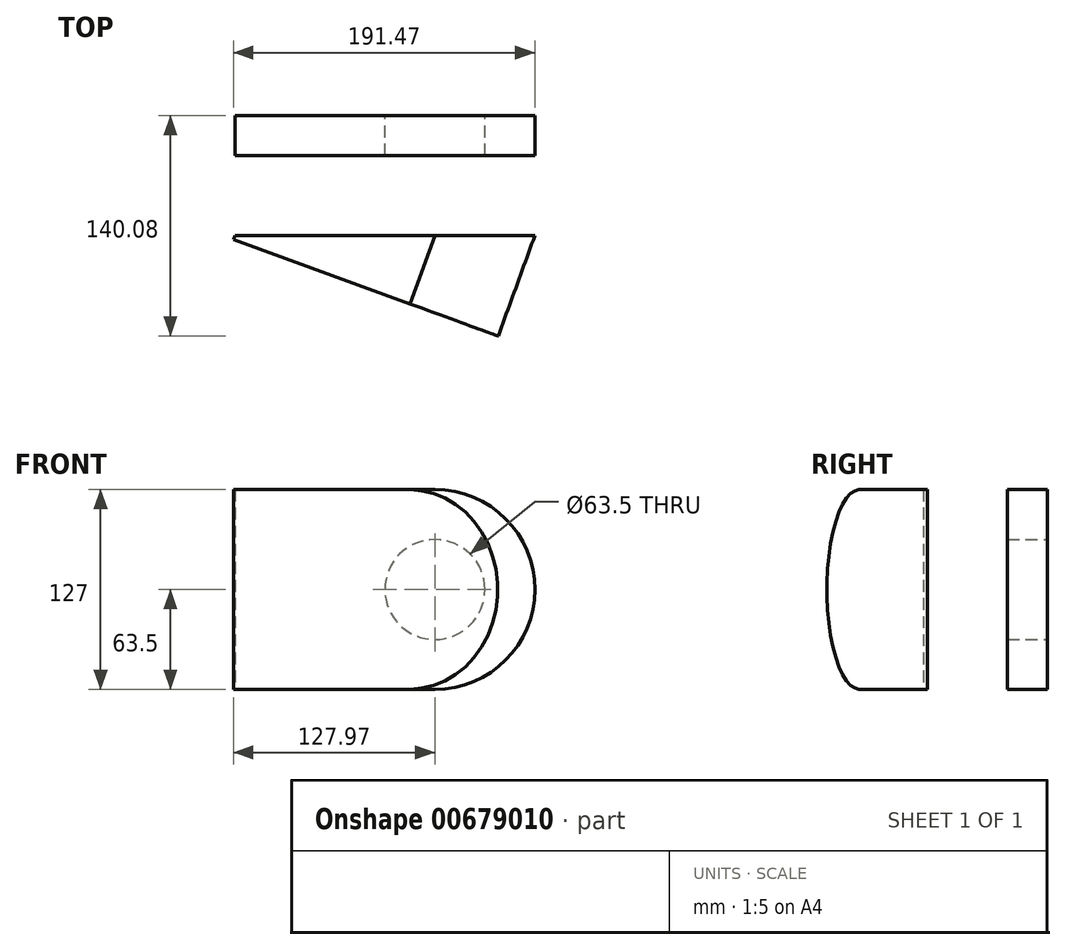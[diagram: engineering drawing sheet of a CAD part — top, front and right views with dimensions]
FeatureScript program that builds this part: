
annotation { "Feature Type Name" : "Feature", "Feature Type Description" : "" }
export const myFeature = defineFeature(function(context is Context, id is Id, definition is map)
    precondition{}
    {
        {
            var Q0;
            Q0=qCreatedBy(makeId("Front.planeOp"),FACE);
            var sketch = newSketch(context, id + "F0", { "sketchPlane" : qUnion([Q0])});
            skArc(sketch, "E0", {"start": v(0, -63.5) * mm, "mid": v(63.5, 0) * mm, "end": v(0, 63.5) * mm});
            skCircle(sketch, "E1", {"center": v(0, 0) * mm, "radius": 31.75 * mm});
            skLineSegment(sketch, "E2", {"start": v(0, 63.5) * mm, "end": v(-127, 63.5) * mm});
            skLineSegment(sketch, "E3", {"start": v(-127, 63.5) * mm, "end": v(-127, -63.5) * mm});
            skLineSegment(sketch, "E4", {"start": v(-127, -63.5) * mm, "end": v(0, -63.5) * mm});
            skSolve(sketch);
        }
        {
            var Q0;
            Q0=makeQuery(id+"F0.imprint","IMPRINT",FACE,{"disambiguationData":[TD([[makeQuery(id+"F0.imprint","IMPRINT",EDGE,{"derivedFrom":sQuery(id+"F0.wireOp",EDGE,"E0")}),1.0]])]});
            extrude(context, id + "F1", {"entities" : qUnion([Q0]), "depth" : 25.4 * mm, "offsetDistance" : 25.4 * mm});
        }
        {
            var Q0;
            Q0=makeQuery(id+"F1.opExtrude","CAP_FACE",FACE,{"disambiguationData":[OSD([sQuery(id+"F0.wireOp",EDGE,"E0"),sQuery(id+"F0.wireOp",EDGE,"E1"),sQuery(id+"F0.wireOp",EDGE,"E2"),sQuery(id+"F0.wireOp",EDGE,"E3"),sQuery(id+"F0.wireOp",EDGE,"E4")])],"isStart":false});
            cPlane(context, id + "F2", {"entities" : qUnion([Q0]), "cplaneType" : CPlaneType.OFFSET, "offset" : 50.8 * mm, "width" : 152.4 * mm, "height" : 152.4 * mm});
        }
        {
            var Q0;
            Q0=qCreatedBy(id+"F2.planeOp",FACE);
            var sketch = newSketch(context, id + "F3", { "sketchPlane" : qUnion([Q0])});
            skLineSegment(sketch, "E5.0.0", {"start": v(-127, 63.5) * mm, "end": v(-127, -63.5) * mm});
            skLineSegment(sketch, "E5.0.1", {"start": v(-127, -63.5) * mm, "end": v(0, -63.5) * mm});
            skArc(sketch, "E5.0.2", {"start": v(0, -63.5) * mm, "mid": v(63.5, 0) * mm, "end": v(0, 63.5) * mm});
            skLineSegment(sketch, "E5.0.3", {"start": v(0, 63.5) * mm, "end": v(-127, 63.5) * mm});
            skSolve(sketch);
        }
        {
            var Q0;
            Q0=qCreatedBy(id+"F2.planeOp",FACE);
            var sketch = newSketch(context, id + "F4", { "sketchPlane" : qUnion([Q0])});
            skLineSegment(sketch, "E6", {"start": v(-135.27, 64.96) * mm, "end": v(-135.27, -72.5) * mm, "construction": true});
            skSolve(sketch);
        }
        {
            var Q0;
            Q0=qCreatedBy(id+"F2.planeOp",FACE);
            var Q1;
            Q1=sQuery(id+"F4.wireOp",EDGE,"E6");
            cPlane(context, id + "F5", {"entities" : qUnion([Q0, Q1]), "cplaneType" : CPlaneType.LINE_ANGLE, "offset" : 25.4 * mm, "angle" : 20 * degree, "width" : 152.4 * mm, "height" : 152.4 * mm});
        }
        {
            var Q0;
            Q0=qCreatedBy(id+"F5.planeOp",FACE);
            var sketch = newSketch(context, id + "F6", { "sketchPlane" : qUnion([Q0])});
            skEllipticalArc(sketch, "E7.0.0", {});
            skLineSegment(sketch, "E7.0.1", {"start": v(-26.06, 63.5) * mm, "end": v(93.28, 63.5) * mm});
            skLineSegment(sketch, "E7.0.2", {"start": v(93.28, 63.5) * mm, "end": v(93.28, -63.5) * mm});
            skLineSegment(sketch, "E7.0.3", {"start": v(93.28, -63.5) * mm, "end": v(-26.06, -63.5) * mm});
            const initialGuessF6  = {"E7.0.0": [-0.026061934921415952, 0, 0, 1, 0.0635, 0.059670481419905184, 0, 3.141592653589793]};
            skSetInitialGuess(sketch, initialGuessF6);
            skSolve(sketch);
        }
        {
            var Q0;
            Q0=makeQuery(id+"F3.imprint","IMPRINT",FACE,{"disambiguationData":[TD([[makeQuery(id+"F3.imprint","IMPRINT",EDGE,{"derivedFrom":sQuery(id+"F3.wireOp",EDGE,"E5.0.0")}),1.0]])]});
            var Q1;
            Q1=makeQuery(id+"F6.imprint","IMPRINT",FACE,{"disambiguationData":[TD([[makeQuery(id+"F6.imprint","IMPRINT",EDGE,{"derivedFrom":sQuery(id+"F6.wireOp",EDGE,"E7.0.0")}),1.0]])]});
            loft(context, id + "F7", {"sheetProfilesArray" : [{ "sheetProfileEntities" : qUnion([Q0]) }, { "sheetProfileEntities" : qUnion([Q1]) }]});
        }
    });
